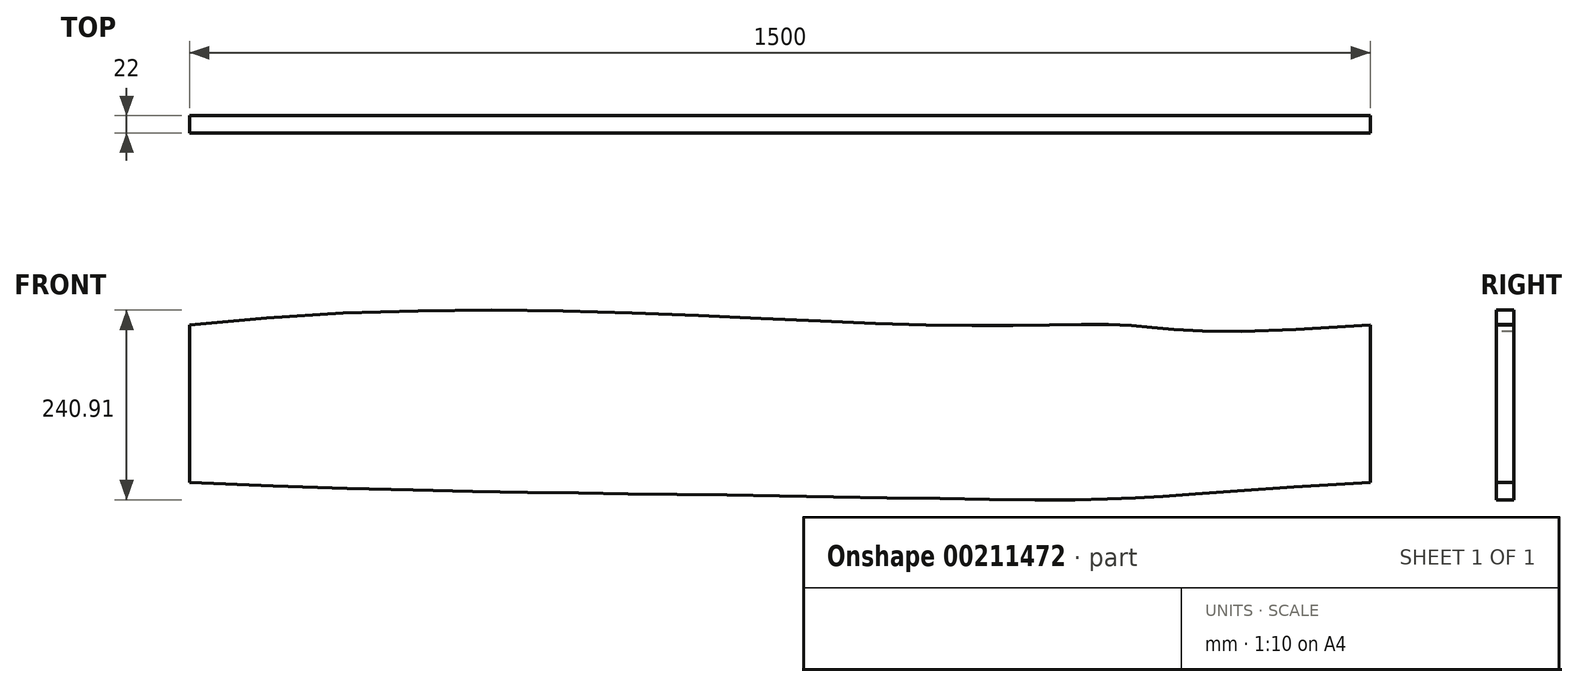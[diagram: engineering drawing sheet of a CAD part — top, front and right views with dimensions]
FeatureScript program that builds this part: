
annotation { "Feature Type Name" : "Feature", "Feature Type Description" : "" }
export const myFeature = defineFeature(function(context is Context, id is Id, definition is map)
    precondition{}
    {
        {
            var Q0;
            Q0=qCreatedBy(makeId("Front.planeOp"),FACE);
            var sketch = newSketch(context, id + "F0", { "sketchPlane" : qUnion([Q0])});
            skLineSegment(sketch, "E0.bottom", {"start": v(778.02, 100) * mm, "end": v(-721.98, 100) * mm, "construction": true});
            skLineSegment(sketch, "E0.top", {"start": v(778.02, -100) * mm, "end": v(-721.98, -100) * mm, "construction": true});
            skLineSegment(sketch, "E0.left", {"start": v(778.02, 100) * mm, "end": v(778.02, -100) * mm, "construction": true});
            skLineSegment(sketch, "E0.right", {"start": v(-721.98, 100) * mm, "end": v(-721.98, -100) * mm, "construction": true});
            skPoint(sketch, "E0.middle", {"position": v(28.02, 0) * mm});
            skLineSegment(sketch, "E1", {"start": v(-721.98, 100) * mm, "end": v(-721.98, -100) * mm});
            skLineSegment(sketch, "E2", {"start": v(778.02, 100) * mm, "end": v(778.02, -100) * mm});
            skFitSpline(sketch, "E3", {"points": [v(-721.98, 100) * mm, v(209.63, 100) * mm, v(465.43, 100) * mm, v(778.02, 100) * mm], "startDerivative": vector(2262.87, 251.46) * mm, "endDerivative": vector(2511.41, 179.87) * mm});
            skFitSpline(sketch, "E4", {"points": [v(-721.98, -100) * mm, v(-34.93, -115.95) * mm, v(423.62, -121.69) * mm, v(778.02, -100) * mm], "startDerivative": vector(2594.1, -107.22) * mm, "endDerivative": vector(2571.13, 143.98) * mm});
            skSolve(sketch);
        }
        {
            var Q0;
            Q0=qSketchRegion(id+"F0",true);
            extrude(context, id + "F1", {"entities" : qUnion([Q0]), "depth" : 22 * mm});
        }
    });
